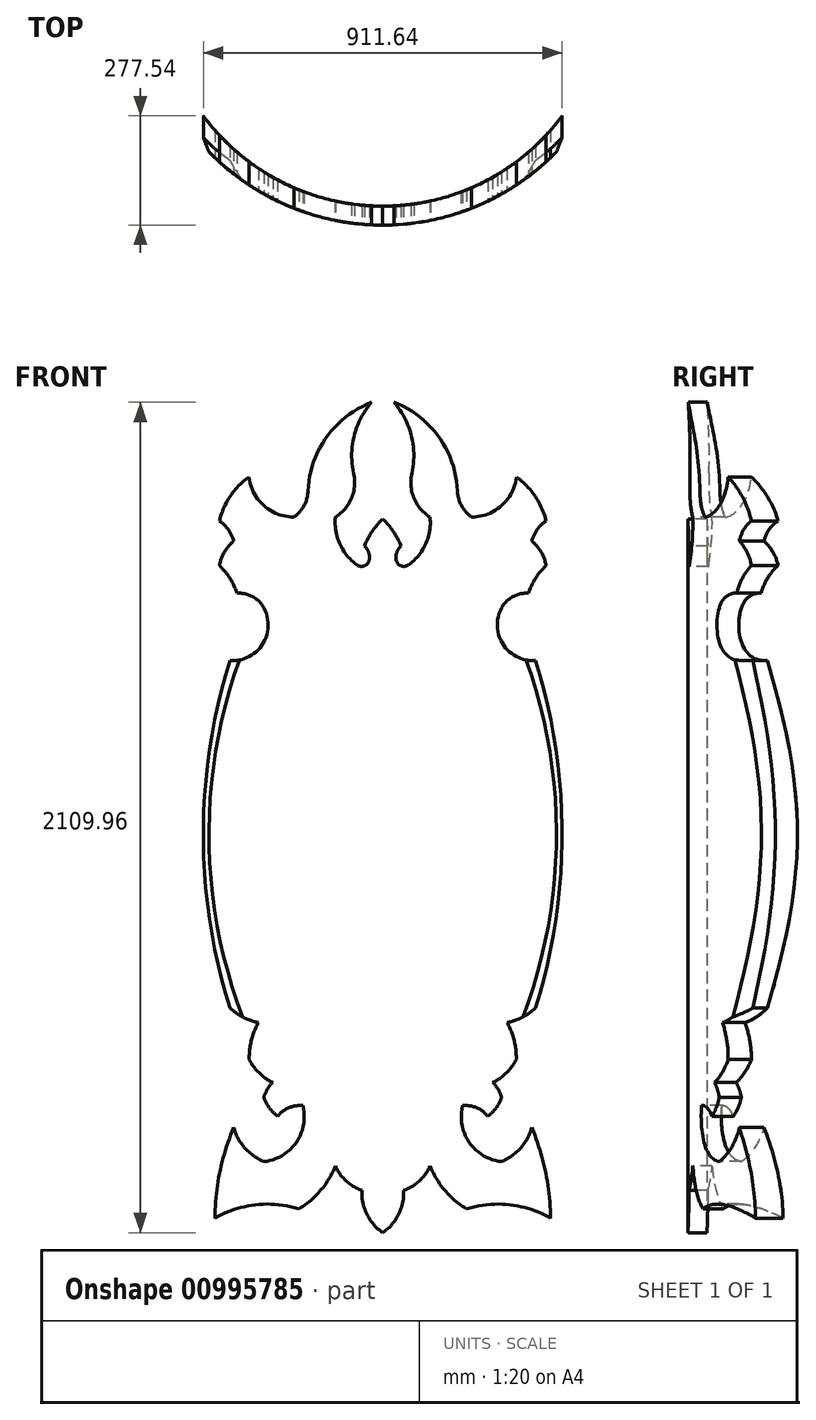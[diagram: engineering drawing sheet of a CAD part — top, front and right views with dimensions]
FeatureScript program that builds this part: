
annotation { "Feature Type Name" : "Feature", "Feature Type Description" : "" }
export const myFeature = defineFeature(function(context is Context, id is Id, definition is map)
    precondition{}
    {
        {
            var Q0;
            Q0=qCreatedBy(makeId("Top.planeOp"),FACE);
            var sketch = newSketch(context, id + "F0", { "sketchPlane" : qUnion([Q0])});
            skArc(sketch, "E0", {"start": v(-457.2, 203.2) * mm, "mid": v(0, 0) * mm, "end": v(457.2, 203.2) * mm});
            skLineSegment(sketch, "E1", {"start": v(0, 0) * mm, "end": v(464.77, 0) * mm, "construction": true});
            skLineSegment(sketch, "E2", {"start": v(-457.2, 203.2) * mm, "end": v(-457.2, 279.4) * mm});
            skLineSegment(sketch, "E3", {"start": v(457.2, 203.2) * mm, "end": v(457.2, 279.4) * mm});
            skArc(sketch, "E4", {"start": v(-457.2, 279.4) * mm, "mid": v(0, 48.24) * mm, "end": v(457.2, 279.4) * mm});
            skSolve(sketch);
        }
        {
            var Q0;
            Q0 = qSketchRegion(id + "F0", true);
            extrude(context, id + "F1", {"entities" : qUnion([Q0]), "depth" : 2133.6 * mm, "offsetDistance" : 25.4 * mm});
        }
        {
            var Q0;
            Q0=qCreatedBy(makeId("Front.planeOp"),FACE);
            var sketch = newSketch(context, id + "F2", { "sketchPlane" : qUnion([Q0])});
            skLineSegment(sketch, "E5", {"start": v(0, 0) * mm, "end": v(0, 2133.6) * mm, "construction": true});
            skArc(sketch, "E6", {"start": v(0, 1813.41) * mm, "mid": v(-26.87, 1781.63) * mm, "end": v(-46.57, 1744.96) * mm});
            skArc(sketch, "E7", {"start": v(-33.93, 1710.08) * mm, "mid": v(-35.9, 1729.1) * mm, "end": v(-46.57, 1744.96) * mm});
            skArc(sketch, "E8", {"start": v(-33.93, 1710.08) * mm, "mid": v(-45.82, 1694.5) * mm, "end": v(-65.32, 1696.56) * mm});
            skArc(sketch, "E9", {"start": v(-65.32, 1696.56) * mm, "mid": v(-109.17, 1749.74) * mm, "end": v(-120.25, 1817.77) * mm});
            skArc(sketch, "E10", {"start": v(-120.25, 1817.77) * mm, "mid": v(-79.26, 1866.26) * mm, "end": v(-73.81, 1929.52) * mm});
            skArc(sketch, "E11", {"start": v(-73.81, 1929.52) * mm, "mid": v(-72.6, 2025.2) * mm, "end": v(-28.18, 2109.96) * mm});
            skArc(sketch, "E12", {"start": v(-28.18, 2109.96) * mm, "mid": v(-142.79, 2021.05) * mm, "end": v(-189.96, 1883.9) * mm});
            skArc(sketch, "E13", {"start": v(-189.96, 1883.9) * mm, "mid": v(-200.05, 1847.16) * mm, "end": v(-225.21, 1818.56) * mm});
            skArc(sketch, "E14", {"start": v(-339.28, 1920.19) * mm, "mid": v(-301.95, 1847.26) * mm, "end": v(-225.21, 1818.56) * mm});
            skArc(sketch, "E15", {"start": v(-339.28, 1920.19) * mm, "mid": v(-387.32, 1871.08) * mm, "end": v(-414.98, 1808.2) * mm});
            skArc(sketch, "E16", {"start": v(-378.69, 1757.38) * mm, "mid": v(-392.16, 1786.12) * mm, "end": v(-414.98, 1808.2) * mm});
            skArc(sketch, "E17", {"start": v(-378.69, 1757.38) * mm, "mid": v(-402.28, 1729.45) * mm, "end": v(-414.98, 1695.16) * mm});
            skArc(sketch, "E18", {"start": v(-370.4, 1624.64) * mm, "mid": v(-388.18, 1662.75) * mm, "end": v(-414.98, 1695.16) * mm});
            skArc(sketch, "E19", {"start": v(-301.95, 1587.31) * mm, "mid": v(-330.67, 1616.07) * mm, "end": v(-370.4, 1624.64) * mm});
            skArc(sketch, "E20", {"start": v(-388.02, 1453.54) * mm, "mid": v(-305.54, 1495.04) * mm, "end": v(-301.95, 1587.31) * mm});
            skArc(sketch, "E21", {"start": v(-388.02, 1453.54) * mm, "mid": v(-455.82, 1012.17) * mm, "end": v(-388.02, 570.8) * mm});
            skArc(sketch, "E22", {"start": v(-388.02, 570.8) * mm, "mid": v(-354.58, 547.31) * mm, "end": v(-316, 533.88) * mm});
            skArc(sketch, "E23", {"start": v(-316, 533.88) * mm, "mid": v(-333.74, 488.47) * mm, "end": v(-339.28, 440.02) * mm});
            skArc(sketch, "E24", {"start": v(-339.28, 440.02) * mm, "mid": v(-314.06, 405.84) * mm, "end": v(-279.33, 381.36) * mm});
            skArc(sketch, "E25", {"start": v(-279.33, 381.36) * mm, "mid": v(-293.5, 364) * mm, "end": v(-301.95, 343.23) * mm});
            skArc(sketch, "E26", {"start": v(-301.95, 343.23) * mm, "mid": v(-288.04, 316.79) * mm, "end": v(-266.78, 295.78) * mm});
            skArc(sketch, "E27", {"start": v(-203.13, 322.81) * mm, "mid": v(-238.44, 317.5) * mm, "end": v(-266.78, 295.78) * mm});
            skArc(sketch, "E28", {"start": v(-301.95, 180.68) * mm, "mid": v(-219.8, 228.97) * mm, "end": v(-203.13, 322.81) * mm});
            skArc(sketch, "E29", {"start": v(-378.69, 267) * mm, "mid": v(-350.21, 215.05) * mm, "end": v(-301.95, 180.68) * mm});
            skArc(sketch, "E30", {"start": v(-378.69, 267) * mm, "mid": v(-413.78, 154.23) * mm, "end": v(-426.36, 36.8) * mm});
            skArc(sketch, "E31", {"start": v(-212.72, 60.34) * mm, "mid": v(-322, 70.94) * mm, "end": v(-426.36, 36.8) * mm});
            skArc(sketch, "E32", {"start": v(-212.72, 60.34) * mm, "mid": v(-157.85, 107.5) * mm, "end": v(-120.29, 169.34) * mm});
            skArc(sketch, "E33", {"start": v(-120.29, 169.34) * mm, "mid": v(-93.13, 131.42) * mm, "end": v(-53.14, 107.43) * mm});
            skArc(sketch, "E34", {"start": v(-53.14, 107.43) * mm, "mid": v(-40.34, 46.9) * mm, "end": v(0, 0) * mm});
            skArc(sketch, "E35.MirrorCS", {"start": v(0, 1813.41) * mm, "mid": v(26.87, 1781.63) * mm, "end": v(46.57, 1744.96) * mm});
            skArc(sketch, "E36.MirrorCS", {"start": v(33.93, 1710.08) * mm, "mid": v(35.9, 1729.1) * mm, "end": v(46.57, 1744.96) * mm});
            skArc(sketch, "E37.MirrorCS", {"start": v(33.93, 1710.08) * mm, "mid": v(45.82, 1694.5) * mm, "end": v(65.32, 1696.56) * mm});
            skArc(sketch, "E38.MirrorCS", {"start": v(65.32, 1696.56) * mm, "mid": v(109.17, 1749.74) * mm, "end": v(120.25, 1817.77) * mm});
            skArc(sketch, "E39.MirrorCS", {"start": v(120.25, 1817.77) * mm, "mid": v(79.26, 1866.26) * mm, "end": v(73.81, 1929.52) * mm});
            skArc(sketch, "E40.MirrorCS", {"start": v(73.81, 1929.52) * mm, "mid": v(72.6, 2025.2) * mm, "end": v(28.18, 2109.96) * mm});
            skArc(sketch, "E41.MirrorCS", {"start": v(28.18, 2109.96) * mm, "mid": v(142.79, 2021.05) * mm, "end": v(189.96, 1883.9) * mm});
            skArc(sketch, "E42.MirrorCS", {"start": v(189.96, 1883.9) * mm, "mid": v(200.05, 1847.16) * mm, "end": v(225.21, 1818.56) * mm});
            skArc(sketch, "E43.MirrorCS", {"start": v(339.28, 1920.19) * mm, "mid": v(301.95, 1847.26) * mm, "end": v(225.21, 1818.56) * mm});
            skArc(sketch, "E44.MirrorCS", {"start": v(339.28, 1920.19) * mm, "mid": v(387.32, 1871.08) * mm, "end": v(414.98, 1808.2) * mm});
            skArc(sketch, "E45.MirrorCS", {"start": v(378.69, 1757.38) * mm, "mid": v(392.16, 1786.12) * mm, "end": v(414.98, 1808.2) * mm});
            skArc(sketch, "E46.MirrorCS", {"start": v(378.69, 1757.38) * mm, "mid": v(402.28, 1729.45) * mm, "end": v(414.98, 1695.16) * mm});
            skArc(sketch, "E47.MirrorCS", {"start": v(370.4, 1624.64) * mm, "mid": v(388.18, 1662.75) * mm, "end": v(414.98, 1695.16) * mm});
            skArc(sketch, "E48.MirrorCS", {"start": v(301.95, 1587.31) * mm, "mid": v(330.67, 1616.07) * mm, "end": v(370.4, 1624.64) * mm});
            skArc(sketch, "E49.MirrorCS", {"start": v(388.02, 1453.54) * mm, "mid": v(305.54, 1495.04) * mm, "end": v(301.95, 1587.31) * mm});
            skArc(sketch, "E50.MirrorCS", {"start": v(388.02, 1453.54) * mm, "mid": v(455.82, 1012.17) * mm, "end": v(388.02, 570.8) * mm});
            skArc(sketch, "E51.MirrorCS", {"start": v(388.02, 570.8) * mm, "mid": v(354.58, 547.31) * mm, "end": v(316, 533.88) * mm});
            skArc(sketch, "E52.MirrorCS", {"start": v(316, 533.88) * mm, "mid": v(333.74, 488.47) * mm, "end": v(339.28, 440.02) * mm});
            skArc(sketch, "E53.MirrorCS", {"start": v(339.28, 440.02) * mm, "mid": v(314.06, 405.84) * mm, "end": v(279.33, 381.36) * mm});
            skArc(sketch, "E54.MirrorCS", {"start": v(279.33, 381.36) * mm, "mid": v(293.5, 364) * mm, "end": v(301.95, 343.23) * mm});
            skArc(sketch, "E55.MirrorCS", {"start": v(301.95, 343.23) * mm, "mid": v(288.04, 316.79) * mm, "end": v(266.78, 295.78) * mm});
            skArc(sketch, "E56.MirrorCS", {"start": v(203.13, 322.81) * mm, "mid": v(238.44, 317.5) * mm, "end": v(266.78, 295.78) * mm});
            skArc(sketch, "E57.MirrorCS", {"start": v(301.95, 180.68) * mm, "mid": v(219.8, 228.97) * mm, "end": v(203.13, 322.81) * mm});
            skArc(sketch, "E58.MirrorCS", {"start": v(378.69, 267) * mm, "mid": v(350.21, 215.05) * mm, "end": v(301.95, 180.68) * mm});
            skArc(sketch, "E59.MirrorCS", {"start": v(378.69, 267) * mm, "mid": v(413.78, 154.23) * mm, "end": v(426.36, 36.8) * mm});
            skArc(sketch, "E60.MirrorCS", {"start": v(212.72, 60.34) * mm, "mid": v(322, 70.94) * mm, "end": v(426.36, 36.8) * mm});
            skArc(sketch, "E61.MirrorCS", {"start": v(212.72, 60.34) * mm, "mid": v(157.85, 107.5) * mm, "end": v(120.29, 169.34) * mm});
            skArc(sketch, "E62.MirrorCS", {"start": v(120.29, 169.34) * mm, "mid": v(93.13, 131.42) * mm, "end": v(53.14, 107.43) * mm});
            skArc(sketch, "E63.MirrorCS", {"start": v(53.14, 107.43) * mm, "mid": v(40.34, 46.9) * mm, "end": v(0, 0) * mm});
            skCircle(sketch, "E64", {"center": v(0, 1066.8) * mm, "radius": 1394.52 * mm});
            skSolve(sketch);
        }
        {
            var Q0;
            Q0 = qSketchRegion(id + "F2", true);
            extrude(context, id + "F3", {"entities" : qUnion([Q0]), "operationType" : NewBodyOperationType.REMOVE, "endBound" : BoundingType.THROUGH_ALL, "oppositeDirection" : true, "depth" : 25.4 * mm, "offsetDistance" : 25.4 * mm});
        }
        {
            var Q0;
            Q0=makeQuery(id+"F3.boolean.opBoolean","INTERSECT",EDGE,{"derivedFrom":[makeQuery(id+"F1.opExtrude","SWEPT_FACE",FACE,{"disambiguationData":[OSD([sQuery(id+"F0.wireOp",EDGE,"E0")])]}),makeQuery(id+"F3.opExtrude","SWEPT_FACE",FACE,{"disambiguationData":[OSD([sQuery(id+"F2.wireOp",EDGE,"E21")])]})]});
            var Q1;
            Q1=makeQuery(id+"F3.boolean.opBoolean","INTERSECT",EDGE,{"derivedFrom":[makeQuery(id+"F1.opExtrude","SWEPT_FACE",FACE,{"disambiguationData":[OSD([sQuery(id+"F0.wireOp",EDGE,"E0")])]}),makeQuery(id+"F3.opExtrude","SWEPT_FACE",FACE,{"disambiguationData":[OSD([sQuery(id+"F2.wireOp",EDGE,"E50.MirrorCS")])]})]});
            chamfer(context, id + "F4", {"entities" : qUnion([Q0, Q1]), "width" : 50.8 * mm, "tangentPropagation" : true});
        }
    });
